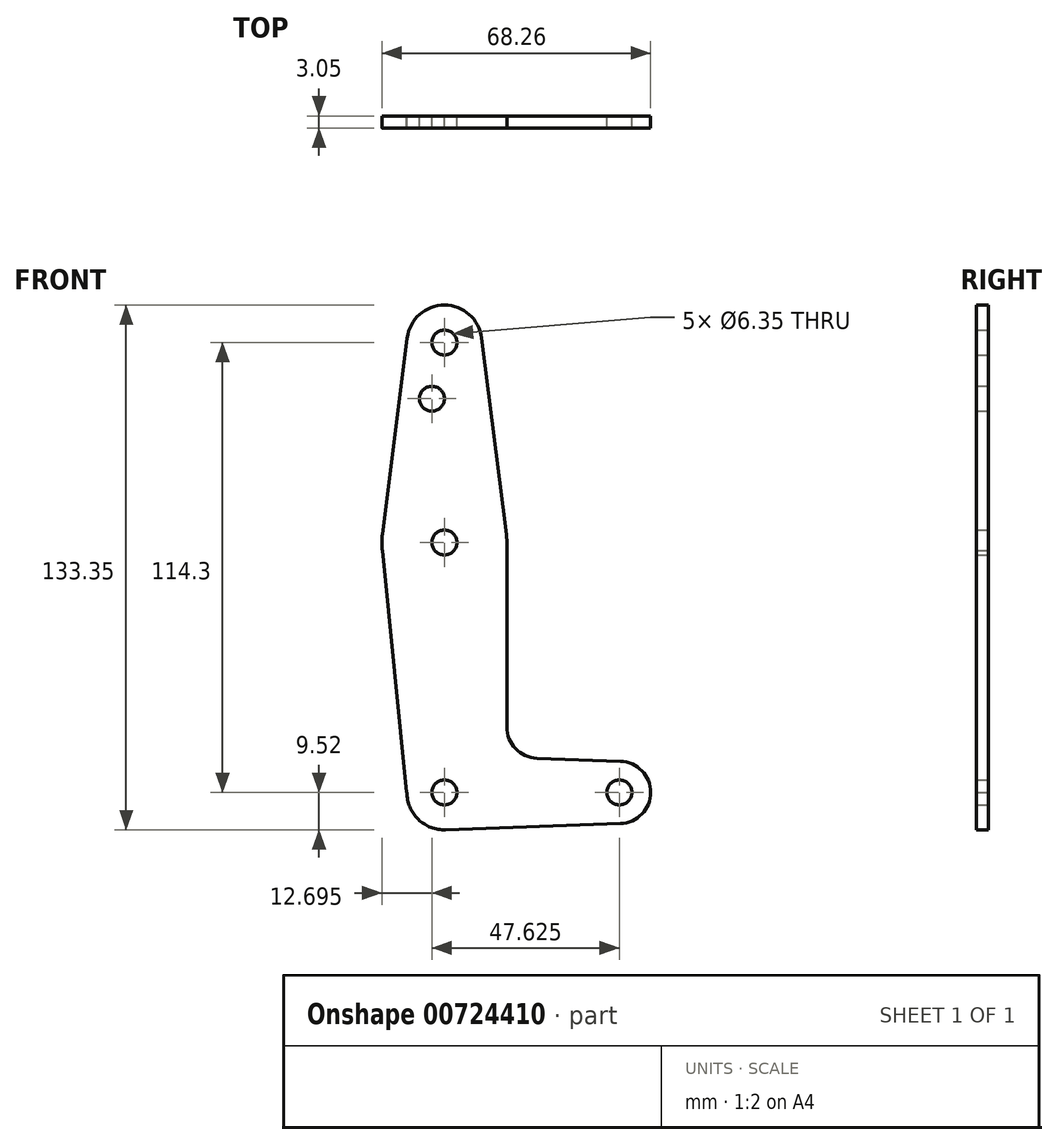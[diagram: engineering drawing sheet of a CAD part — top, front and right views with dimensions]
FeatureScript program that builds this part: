
annotation { "Feature Type Name" : "Feature", "Feature Type Description" : "" }
export const myFeature = defineFeature(function(context is Context, id is Id, definition is map)
    precondition{}
    {
        {
            var Q0;
            Q0=qCreatedBy(makeId("Front.planeOp"),FACE);
            var sketch = newSketch(context, id + "F0", { "sketchPlane" : qUnion([Q0])});
            skLineSegment(sketch, "E0", {"start": v(0, 0) * mm, "end": v(0, 114.3) * mm, "construction": true});
            skLineSegment(sketch, "E1", {"start": v(0, 0) * mm, "end": v(44.45, 0) * mm, "construction": true});
            skCircle(sketch, "E2", {"center": v(0, 0) * mm, "radius": 9.53 * mm});
            skCircle(sketch, "E3", {"center": v(0, 114.3) * mm, "radius": 9.53 * mm});
            skCircle(sketch, "E4", {"center": v(44.45, 0) * mm, "radius": 7.94 * mm});
            skCircle(sketch, "E5", {"center": v(0, 63.5) * mm, "radius": 15.88 * mm});
            skLineSegment(sketch, "E6", {"start": v(-9.45, 115.5) * mm, "end": v(-15.75, 65.48) * mm});
            skLineSegment(sketch, "E7", {"start": v(-15.75, 61.52) * mm, "end": v(-9.57, 0) * mm});
            skLineSegment(sketch, "E8", {"start": v(9.45, 115.5) * mm, "end": v(15.75, 65.48) * mm});
            skLineSegment(sketch, "E9", {"start": v(15.88, 63.5) * mm, "end": v(15.88, 16.63) * mm});
            skLineSegment(sketch, "E10", {"start": v(-9.57, 0) * mm, "end": v(9.52, 0) * mm});
            skLineSegment(sketch, "E11", {"start": v(23.54, 8.69) * mm, "end": v(44.73, 7.93) * mm});
            skLineSegment(sketch, "E12", {"start": v(44.73, -7.93) * mm, "end": v(0, -9.53) * mm});
            skCircle(sketch, "E13", {"center": v(0, 114.3) * mm, "radius": 3.18 * mm});
            skCircle(sketch, "E14", {"center": v(-3.17, 100.03) * mm, "radius": 3.18 * mm});
            skCircle(sketch, "E15", {"center": v(0, 63.5) * mm, "radius": 3.18 * mm});
            skCircle(sketch, "E16", {"center": v(0, 0) * mm, "radius": 3.18 * mm});
            skCircle(sketch, "E17", {"center": v(44.45, 0) * mm, "radius": 3.18 * mm});
            skArc(sketch, "E18.filletArc", {"start": v(15.88, 16.63) * mm, "mid": v(18.1, 11.11) * mm, "end": v(23.54, 8.69) * mm});
            skSolve(sketch);
        }
        {
            var Q0;
            Q0 = qSketchRegion(id + "F0", true);
            extrude(context, id + "F1", {"entities" : qUnion([Q0]), "depth" : 3.05 * mm, "offsetDistance" : 25.4 * mm});
        }
    });
